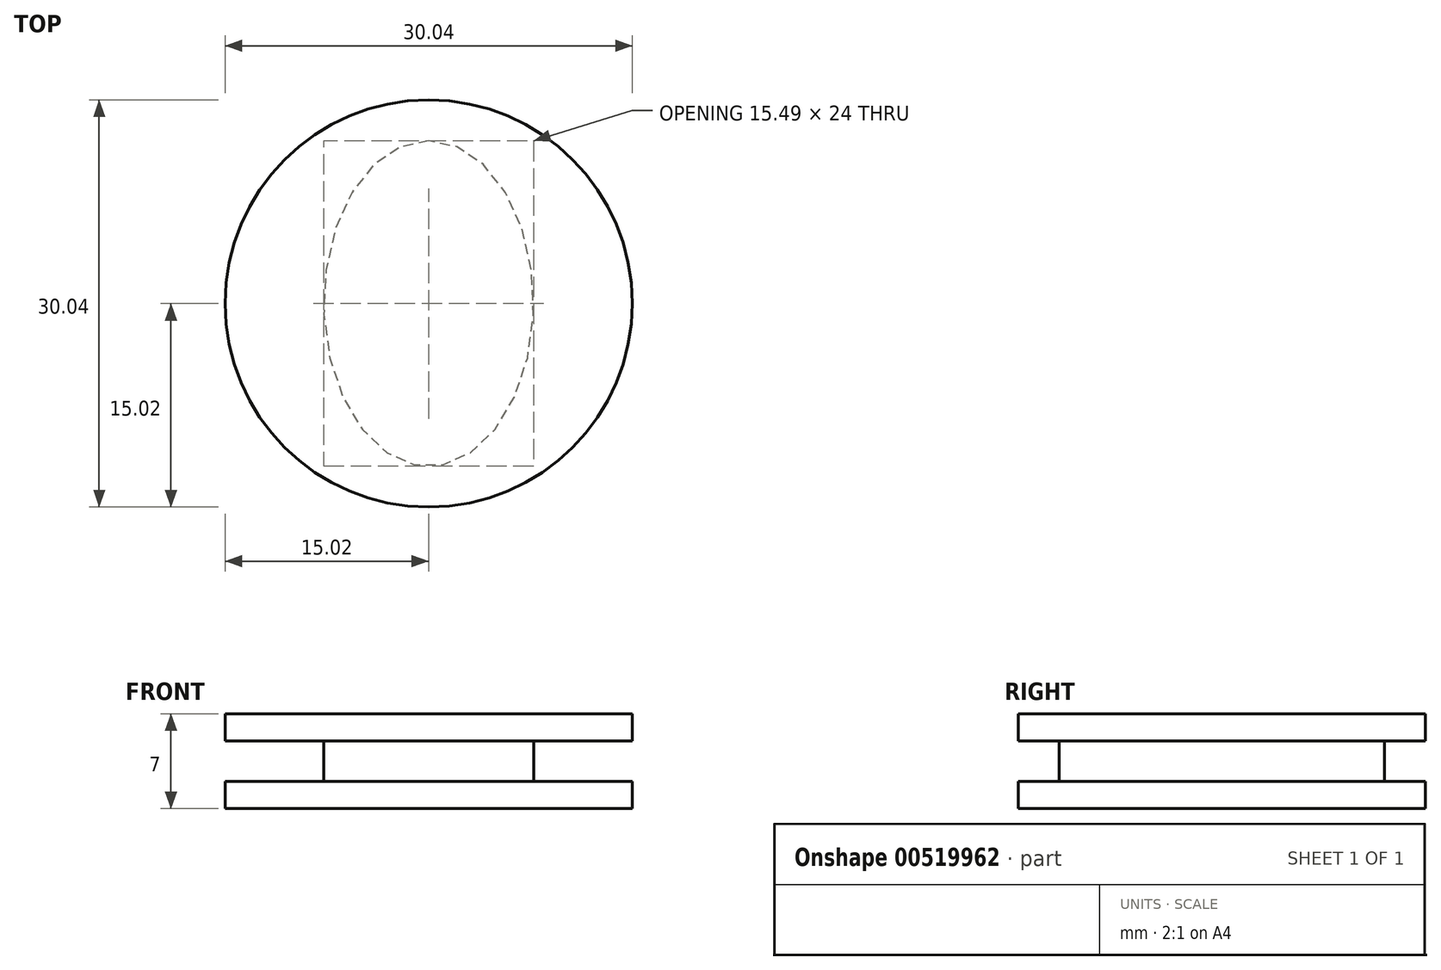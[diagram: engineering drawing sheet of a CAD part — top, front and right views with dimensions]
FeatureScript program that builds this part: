
annotation { "Feature Type Name" : "Feature", "Feature Type Description" : "" }
export const myFeature = defineFeature(function(context is Context, id is Id, definition is map)
    precondition{}
    {
        {
            var Q0;
            Q0=qCreatedBy(makeId("Top.planeOp"),FACE);
            var sketch = newSketch(context, id + "F0", { "sketchPlane" : qUnion([Q0])});
            skCircle(sketch, "E0", {"center": v(0, 0) * mm, "radius": 15.02 * mm});
            skSolve(sketch);
        }
        {
            var Q0;
            Q0 = qSketchRegion(id + "F0", true);
            extrude(context, id + "F1", {"entities" : qUnion([Q0]), "depth" : 2 * mm, "offsetDistance" : 25 * mm});
        }
        {
            var Q0;
            Q0=makeQuery(id+"F1.opExtrude","CAP_FACE",FACE,{"disambiguationData":[OSD([sQuery(id+"F0.wireOp",EDGE,"E0")])],"isStart":false});
            var sketch = newSketch(context, id + "F2", { "sketchPlane" : qUnion([Q0])});
            skEllipse(sketch, "E1", {"center": v(0, 0) * mm, "majorRadius": 12 * mm, "minorRadius": 7.75 * mm, "majorAxis": v(0, 1)});
            skSolve(sketch);
        }
        {
            var Q0;
            Q0 = qSketchRegion(id + "F2", true);
            extrude(context, id + "F3", {"entities" : qUnion([Q0]), "operationType" : NewBodyOperationType.ADD, "depth" : 1.5 * mm, "offsetDistance" : 25 * mm});
        }
        {
            var Q0;
            Q0=qCreatedBy(makeId("Top.planeOp"),FACE);
            cPlane(context, id + "F4", {"entities" : qUnion([Q0]), "cplaneType" : CPlaneType.OFFSET, "offset" : 3.5 * mm, "width" : 150 * mm, "height" : 150 * mm});
        }
        {
            var Q0;
            Q0=makeQuery(id+"F1.opExtrude","SWEPT_BODY",BODY,{"disambiguationData":[OSD([sQuery(id+"F0.wireOp",EDGE,"E0")])]});
            var Q1;
            Q1=qCreatedBy(id+"F4.planeOp",FACE);
            mirror(context, id + "F5", {"operationType" : NewBodyOperationType.ADD, "entities" : qUnion([Q0]), "mirrorPlane" : qUnion([Q1])});
        }
    });
